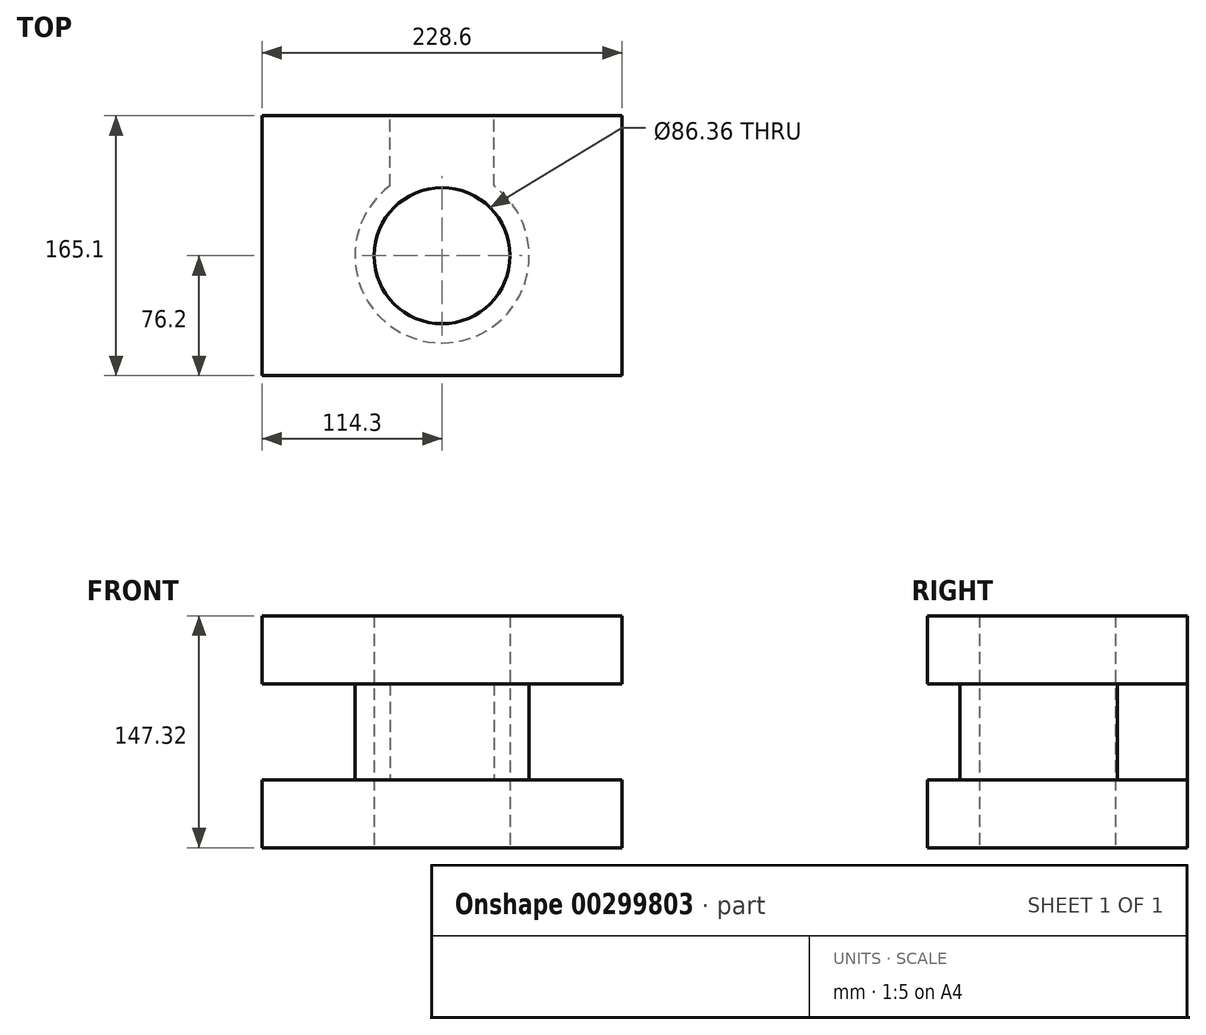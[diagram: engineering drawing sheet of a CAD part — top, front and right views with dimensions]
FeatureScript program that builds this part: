
annotation { "Feature Type Name" : "Feature", "Feature Type Description" : "" }
export const myFeature = defineFeature(function(context is Context, id is Id, definition is map)
    precondition{}
    {
        {
            var Q0;
            Q0=qCreatedBy(makeId("Top.planeOp"),FACE);
            var sketch = newSketch(context, id + "F0", { "sketchPlane" : qUnion([Q0])});
            skLineSegment(sketch, "E0.bottom", {"start": v(-114.3, -82.55) * mm, "end": v(114.3, -82.55) * mm});
            skLineSegment(sketch, "E0.top", {"start": v(-114.3, 82.55) * mm, "end": v(114.3, 82.55) * mm});
            skLineSegment(sketch, "E0.left", {"start": v(-114.3, -82.55) * mm, "end": v(-114.3, 82.55) * mm});
            skLineSegment(sketch, "E0.right", {"start": v(114.3, -82.55) * mm, "end": v(114.3, 82.55) * mm});
            skCircle(sketch, "E1", {"center": v(0, -6.35) * mm, "radius": 43.18 * mm});
            skArc(sketch, "E2", {"start": v(0, -61.72) * mm, "mid": v(52.57, -23.74) * mm, "end": v(33.02, 38.1) * mm});
            skLineSegment(sketch, "E3", {"start": v(33.02, 38.1) * mm, "end": v(33.02, 82.55) * mm});
            skLineSegment(sketch, "E4", {"start": v(0, 66.88) * mm, "end": v(0, 82.55) * mm});
            skPoint(sketch, "E4.startSnap0", {"position": v(0, 82.55) * mm});
            skLineSegment(sketch, "E5.MirrorCS", {"start": v(-33.02, 38.1) * mm, "end": v(-33.02, 82.55) * mm});
            skArc(sketch, "E6.MirrorCS", {"start": v(0, -61.72) * mm, "mid": v(-52.57, -23.74) * mm, "end": v(-33.02, 38.1) * mm});
            skLineSegment(sketch, "E7", {"start": v(-33.02, 82.55) * mm, "end": v(33.02, 82.55) * mm});
            skSolve(sketch);
        }
        {
            var Q0;
            Q0 = qSketchRegion(id + "F0", true);
            extrude(context, id + "F1", {"entities" : qUnion([Q0]), "depth" : 147.32 * mm});
        }
        {
            var Q0;
            Q0=makeQuery(id+"F0.imprint","IMPRINT",FACE,{"disambiguationData":[TD([[makeQuery(id+"F0.imprint","IMPRINT",EDGE,{"derivedFrom":sQuery(id+"F0.wireOp",EDGE,"E0.bottom")}),1.0]])]});
            extrude(context, id + "F2", {"entities" : qUnion([Q0]), "operationType" : NewBodyOperationType.REMOVE, "depth" : 104.14 * mm});
        }
        {
            var Q0;
            Q0=makeQuery(id+"F0.imprint","IMPRINT",FACE,{"disambiguationData":[TD([[makeQuery(id+"F0.imprint","IMPRINT",EDGE,{"derivedFrom":sQuery(id+"F0.wireOp",EDGE,"E0.bottom")}),1.0]])]});
            extrude(context, id + "F3", {"entities" : qUnion([Q0]), "operationType" : NewBodyOperationType.ADD, "depth" : 43.18 * mm});
        }
    });
